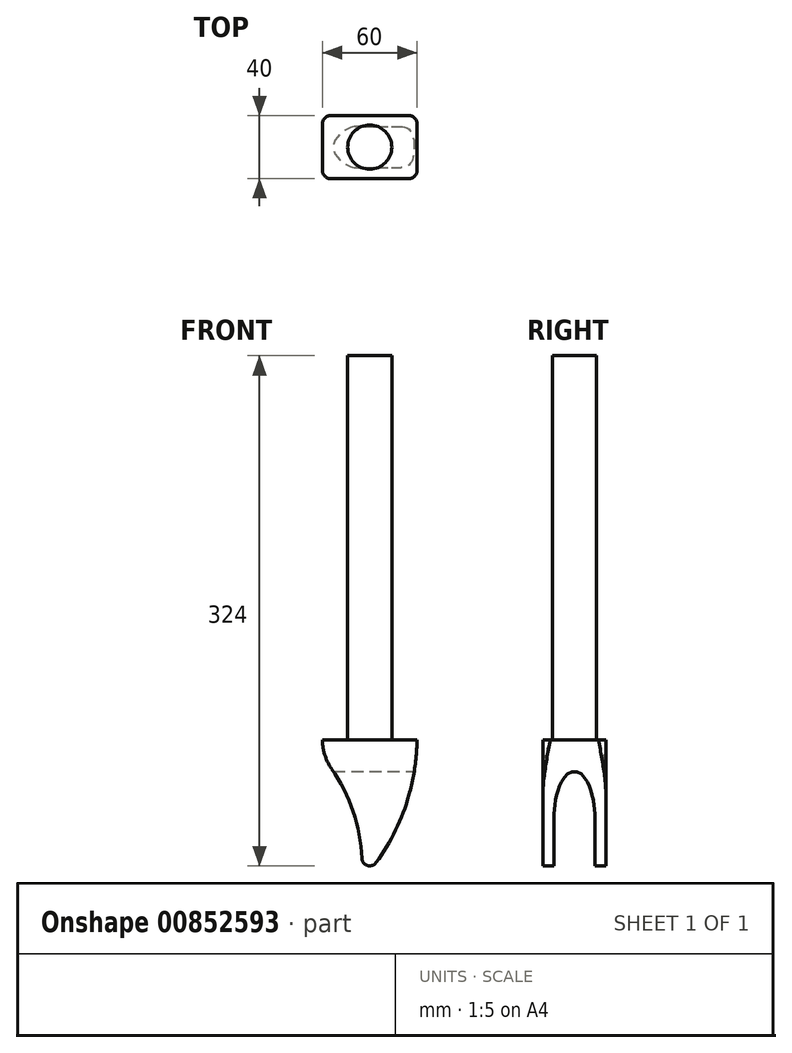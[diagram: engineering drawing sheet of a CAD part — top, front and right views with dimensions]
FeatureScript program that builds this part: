
annotation { "Feature Type Name" : "Feature", "Feature Type Description" : "" }
export const myFeature = defineFeature(function(context is Context, id is Id, definition is map)
    precondition{}
    {
        {
            var Q0;
            Q0=qCreatedBy(makeId("Top.planeOp"),FACE);
            var sketch = newSketch(context, id + "F0", { "sketchPlane" : qUnion([Q0])});
            skCircle(sketch, "E0", {"center": v(0, 0) * mm, "radius": 14 * mm});
            skSolve(sketch);
        }
        {
            var Q0;
            Q0 = qSketchRegion(id + "F0", true);
            extrude(context, id + "F1", {"entities" : qUnion([Q0]), "depth" : 244 * mm, "offsetDistance" : 25 * mm});
        }
        {
            var Q0;
            Q0=qCreatedBy(makeId("Top.planeOp"),FACE);
            var sketch = newSketch(context, id + "F2", { "sketchPlane" : qUnion([Q0])});
            skLineSegment(sketch, "E1.bottom", {"start": v(-30, 20) * mm, "end": v(30, 20) * mm});
            skLineSegment(sketch, "E1.top", {"start": v(-30, -20) * mm, "end": v(30, -20) * mm});
            skLineSegment(sketch, "E1.left", {"start": v(-30, 20) * mm, "end": v(-30, -20) * mm});
            skLineSegment(sketch, "E1.right", {"start": v(30, 20) * mm, "end": v(30, -20) * mm});
            skPoint(sketch, "E1.middle", {"position": v(0, 0) * mm});
            skSolve(sketch);
        }
        {
            var Q0;
            Q0=makeQuery(id+"F2.imprint","IMPRINT",FACE,{"disambiguationData":[TD([[makeQuery(id+"F2.imprint","IMPRINT",EDGE,{"derivedFrom":sQuery(id+"F2.wireOp",EDGE,"E1.bottom")}),-1.0]])]});
            extrude(context, id + "F3", {"entities" : qUnion([Q0]), "operationType" : NewBodyOperationType.ADD, "oppositeDirection" : true, "depth" : 80 * mm, "offsetDistance" : 25 * mm});
        }
        {
            var Q0;
            Q0=makeQuery(id+"F3.opExtrude","SWEPT_EDGE",EDGE,{"disambiguationData":[OSD([sQuery(id+"F2.wireOp",EDGE,"E1.top"),sQuery(id+"F2.wireOp",EDGE,"E1.right")])]});
            var Q1;
            Q1=makeQuery(id+"F3.opExtrude","SWEPT_EDGE",EDGE,{"disambiguationData":[OSD([sQuery(id+"F2.wireOp",EDGE,"E1.bottom"),sQuery(id+"F2.wireOp",EDGE,"E1.right")])]});
            var Q2;
            Q2=makeQuery(id+"F3.opExtrude","SWEPT_EDGE",EDGE,{"disambiguationData":[OSD([sQuery(id+"F2.wireOp",EDGE,"E1.top"),sQuery(id+"F2.wireOp",EDGE,"E1.left")])]});
            var Q3;
            Q3=makeQuery(id+"F3.opExtrude","SWEPT_EDGE",EDGE,{"disambiguationData":[OSD([sQuery(id+"F2.wireOp",EDGE,"E1.bottom"),sQuery(id+"F2.wireOp",EDGE,"E1.left")])]});
            fillet(context, id + "F4", {"entities" : qUnion([Q0, Q1, Q2, Q3]), "radius" : 5 * mm, "tangentPropagation" : true, "allowEdgeOverflow" : false});
        }
        {
            var Q0;
            Q0=qCreatedBy(makeId("Front.planeOp"),FACE);
            var sketch = newSketch(context, id + "F5", { "sketchPlane" : qUnion([Q0])});
            skLineSegment(sketch, "E2.0", {"start": v(-30, -90) * mm, "end": v(-30, 0) * mm});
            skLineSegment(sketch, "E3.0", {"start": v(30, 0) * mm, "end": v(30, -90) * mm});
            skLineSegment(sketch, "E4.1", {"start": v(-25, -80) * mm, "end": v(25, -80) * mm});
            skArc(sketch, "E5", {"start": v(-30, 0) * mm, "mid": v(-28.53, -9.58) * mm, "end": v(-24.26, -18.28) * mm});
            skArc(sketch, "E6", {"start": v(-5, -75.22) * mm, "mid": v(-10.59, -45.38) * mm, "end": v(-24.26, -18.28) * mm});
            skArc(sketch, "E7", {"start": v(4.04, -77.95) * mm, "mid": v(23.1, -41) * mm, "end": v(30, 0) * mm});
            skArc(sketch, "E8", {"start": v(-5, -75.22) * mm, "mid": v(-1.45, -79.79) * mm, "end": v(4.04, -77.95) * mm});
            skLineSegment(sketch, "E9.0", {"start": v(-30, -90) * mm, "end": v(30, -90) * mm});
            skSolve(sketch);
        }
        {
            var Q0;
            Q0 = qSketchRegion(id + "F5", true);
            extrude(context, id + "F6", {"entities" : qUnion([Q0]), "operationType" : NewBodyOperationType.REMOVE, "endBound" : BoundingType.SYMMETRIC, "oppositeDirection" : true, "depth" : 80 * mm, "offsetDistance" : 25 * mm});
        }
        {
            var Q0;
            Q0=qCreatedBy(makeId("Right.planeOp"),FACE);
            var sketch = newSketch(context, id + "F7", { "sketchPlane" : qUnion([Q0])});
            skEllipticalArc(sketch, "E10", {});
            skLineSegment(sketch, "E11", {"start": v(13, -50) * mm, "end": v(13, -80) * mm});
            skLineSegment(sketch, "E12", {"start": v(-13, -50) * mm, "end": v(-13, -80) * mm});
            skLineSegment(sketch, "E13", {"start": v(-13, -80) * mm, "end": v(13, -80) * mm});
            skPoint(sketch, "E14", {"position": v(0, -20) * mm});
            const initialGuessF7  = {"E10": [0, -0.05, 0, -1, 0.03, 0.013, 1.5707963267948966, 4.71238898038469]};
            skSetInitialGuess(sketch, initialGuessF7);
            skSolve(sketch);
        }
        {
            var Q0;
            Q0 = qSketchRegion(id + "F7", true);
            extrude(context, id + "F8", {"entities" : qUnion([Q0]), "operationType" : NewBodyOperationType.REMOVE, "endBound" : BoundingType.SYMMETRIC, "oppositeDirection" : true, "depth" : 70 * mm, "offsetDistance" : 25 * mm});
        }
    });
